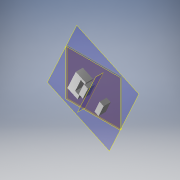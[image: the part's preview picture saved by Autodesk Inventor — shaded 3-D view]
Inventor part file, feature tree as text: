
AUTODESK INVENTOR PART (.ipt)
format: ipt  version: 2019 (Build 230136000, 136)  size: 137,728 bytes
history: native  units: mm
features: plane x4, other x3, extrude x2, sketch x2, reference x1
ambient origin geometry x8: Origin, YZ Plane, XZ Plane, XY Plane, X Axis, Y Axis, Z Axis, Center Point
bodies: Solid1 (feature_tree)
feature tree (12):
  plane  "Work Plane1"
  plane  "Work Plane2"
  extrude  "Extrusion1"  Depth=3.5mm
  plane  "Work Plane3"
  extrude  "Extrusion2"  Depth=3.5mm
  plane  "Arbeitsebene4"
  sketch  "Sketch1"  dims[d0=9.5mm d1=3.5mm]
  reference  "Reference1"
  sketch  "Sketch2"  dims[d2=9.5mm d3=3.5mm d4=0.0mm d5=2.5mm d6=10.0mm d7=0.0mm d8=5.5mm d9=0.0mm d10=5.5mm d11=0.0mm]
  other  "<userpath>\Downloads\cellSTORM\00_KES400.iam"
  other  "00_KES400.iam"
  other  "00_KES400_Bluray_Lens:1"
